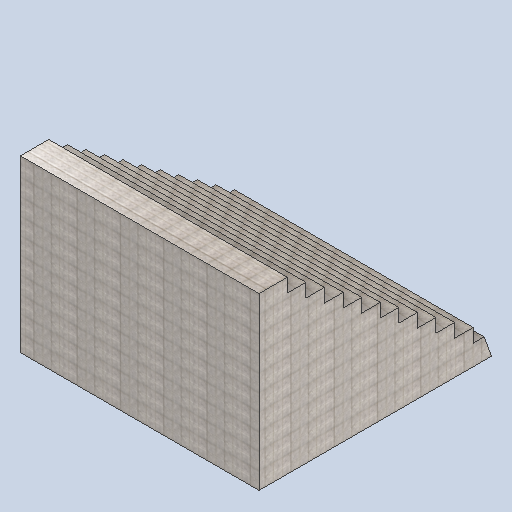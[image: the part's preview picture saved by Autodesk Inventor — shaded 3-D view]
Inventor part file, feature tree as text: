
AUTODESK INVENTOR PART (.ipt)
format: ipt  version: 2024.2 (Build 282272000, 272)  size: 306,176 bytes
history: native  units: in
note: dims shown in document units (in); Inventor stores cm internally (conversion verified against a paired STEP export)
features: other x3, sketch x3
ambient origin geometry x8: Origin, YZ Plane, XZ Plane, XY Plane, X Axis, Y Axis, Z Axis, Center Point
bodies: Solid1 (feature_tree)
feature tree (6):
  other  "side_stair.ipt"
  other  "Solid1::side_stair.ipt"
  other  "TaggingFeature1"
  sketch  "Sketch1"  dims[d0=0.3937in]
  sketch  "Sketch2"
  sketch  "Sketch3"
